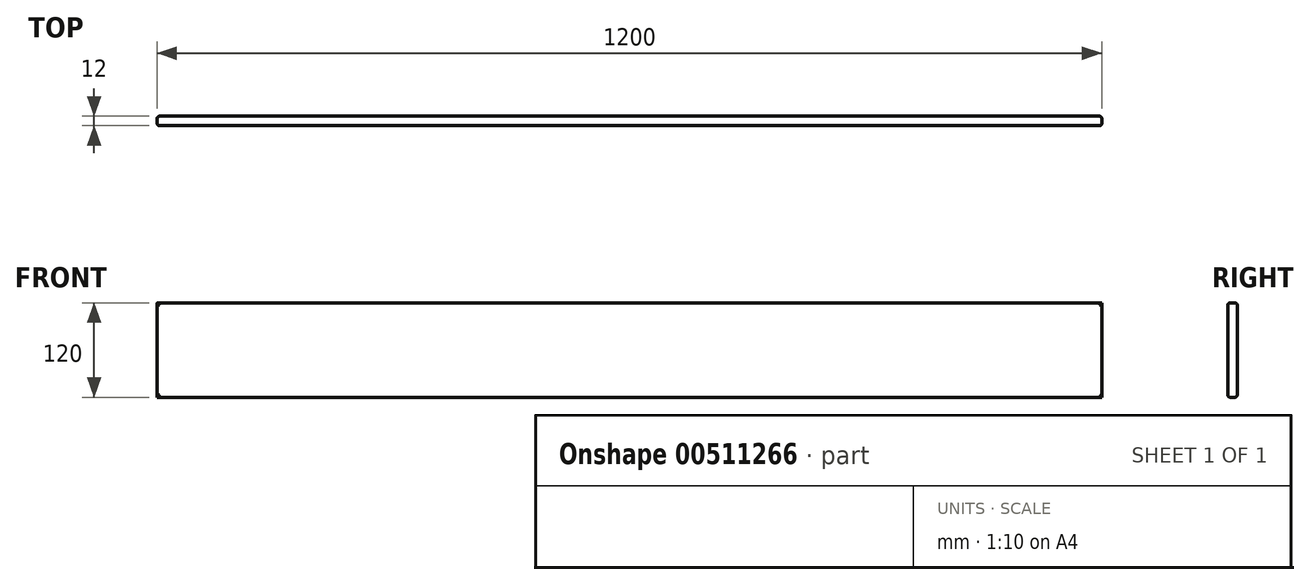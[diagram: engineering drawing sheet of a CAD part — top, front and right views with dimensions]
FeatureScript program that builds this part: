
annotation { "Feature Type Name" : "Feature", "Feature Type Description" : "" }
export const myFeature = defineFeature(function(context is Context, id is Id, definition is map)
    precondition{}
    {
        {
            var Q0;
            Q0=qCreatedBy(makeId("Front.planeOp"),FACE);
            var sketch = newSketch(context, id + "F0", { "sketchPlane" : qUnion([Q0])});
            skLineSegment(sketch, "E0.bottom", {"start": v(-674.1, 6.22) * mm, "end": v(525.9, 6.22) * mm});
            skLineSegment(sketch, "E0.top", {"start": v(-674.1, -113.78) * mm, "end": v(525.9, -113.78) * mm});
            skLineSegment(sketch, "E0.left", {"start": v(-674.1, 6.22) * mm, "end": v(-674.1, -113.78) * mm});
            skLineSegment(sketch, "E0.right", {"start": v(525.9, 6.22) * mm, "end": v(525.9, -113.78) * mm});
            skSolve(sketch);
        }
        {
            var Q0;
            Q0=makeQuery(id+"F0.imprint","IMPRINT",FACE,{"disambiguationData":[TD([[makeQuery(id+"F0.imprint","IMPRINT",EDGE,{"derivedFrom":sQuery(id+"F0.wireOp",EDGE,"E0.bottom")}),-1.0]])]});
            extrude(context, id + "F1", {"entities" : qUnion([Q0]), "depth" : 12 * mm});
        }
        {
            var Q0;
            Q0=makeQuery(id+"F1.opExtrude","CAP_FACE",FACE,{"disambiguationData":[OSD([sQuery(id+"F0.wireOp",EDGE,"E0.bottom"),sQuery(id+"F0.wireOp",EDGE,"E0.top"),sQuery(id+"F0.wireOp",EDGE,"E0.left"),sQuery(id+"F0.wireOp",EDGE,"E0.right")])],"isStart":true});
            var sketch = newSketch(context, id + "F2", { "sketchPlane" : qUnion([Q0])});
            skLineSegment(sketch, "E1", {"start": v(-525.9, 6.22) * mm, "end": v(-525.9, -13.78) * mm});
            skLineSegment(sketch, "E2", {"start": v(-525.9, -13.78) * mm, "end": v(74.1, -13.78) * mm});
            skLineSegment(sketch, "E3", {"start": v(74.1, -13.78) * mm, "end": v(674.1, -13.78) * mm});
            skSolve(sketch);
        }
        {
            var Q0;
            Q0=makeQuery(id+"F1.opExtrude","CAP_FACE",FACE,{"disambiguationData":[OSD([sQuery(id+"F0.wireOp",EDGE,"E0.bottom"),sQuery(id+"F0.wireOp",EDGE,"E0.top"),sQuery(id+"F0.wireOp",EDGE,"E0.left"),sQuery(id+"F0.wireOp",EDGE,"E0.right")])],"isStart":false});
            var Q1;
            Q1=makeQuery(id+"F1.opExtrude","CAP_FACE",FACE,{"disambiguationData":[OSD([sQuery(id+"F0.wireOp",EDGE,"E0.bottom"),sQuery(id+"F0.wireOp",EDGE,"E0.top"),sQuery(id+"F0.wireOp",EDGE,"E0.left"),sQuery(id+"F0.wireOp",EDGE,"E0.right")])],"isStart":true});
            fillet(context, id + "F3", {"entities" : qUnion([Q0, Q1]), "radius" : 3 * mm, "tangentPropagation" : true, "allowEdgeOverflow" : false});
        }
    });
